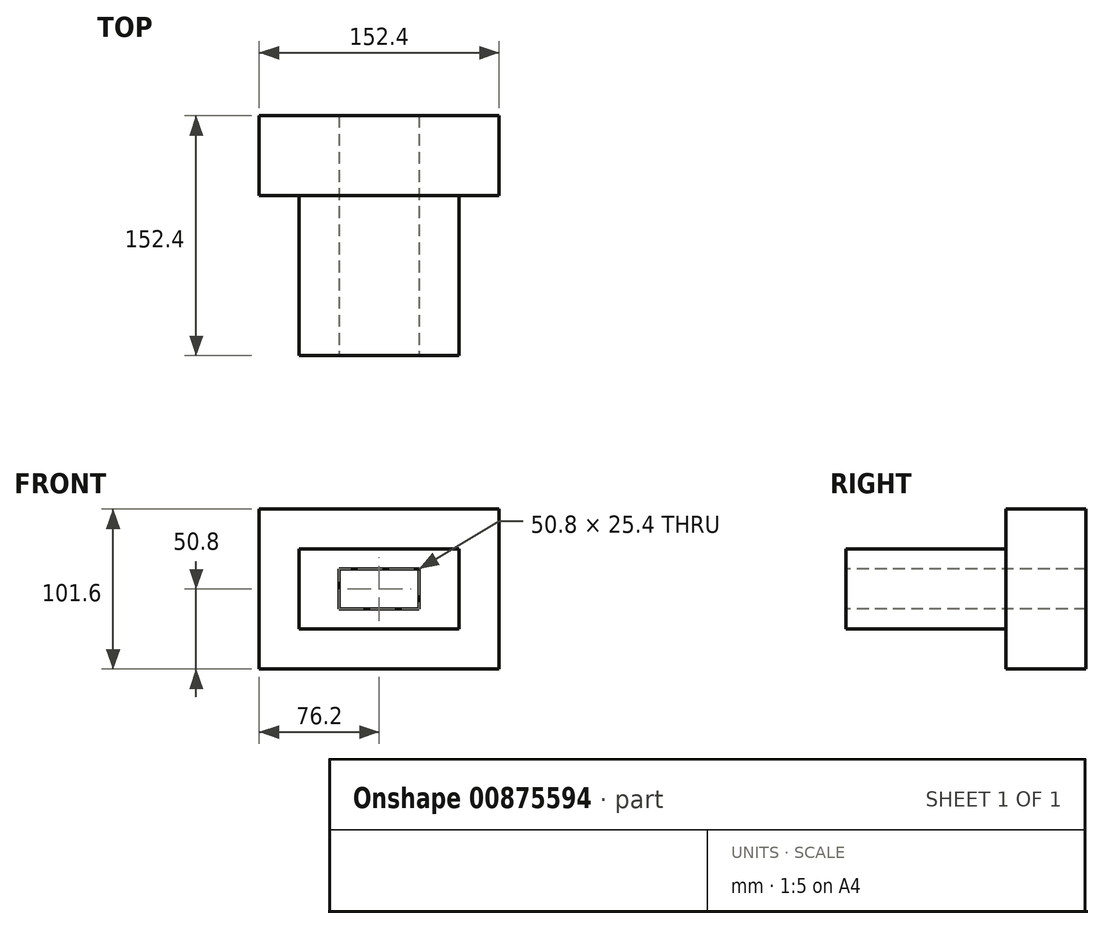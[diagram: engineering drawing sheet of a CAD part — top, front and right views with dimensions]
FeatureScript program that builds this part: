
annotation { "Feature Type Name" : "Feature", "Feature Type Description" : "" }
export const myFeature = defineFeature(function(context is Context, id is Id, definition is map)
    precondition{}
    {
        {
            var Q0;
            Q0=qCreatedBy(makeId("Front.planeOp"),FACE);
            var sketch = newSketch(context, id + "F0", { "sketchPlane" : qUnion([Q0])});
            skLineSegment(sketch, "E0.bottom", {"start": v(-76.2, 50.8) * mm, "end": v(76.2, 50.8) * mm});
            skLineSegment(sketch, "E0.top", {"start": v(-76.2, -50.8) * mm, "end": v(76.2, -50.8) * mm});
            skLineSegment(sketch, "E0.left", {"start": v(-76.2, 50.8) * mm, "end": v(-76.2, -50.8) * mm});
            skLineSegment(sketch, "E0.right", {"start": v(76.2, 50.8) * mm, "end": v(76.2, -50.8) * mm});
            skSolve(sketch);
        }
        {
            var Q0;
            Q0 = qSketchRegion(id + "F0", true);
            extrude(context, id + "F1", {"entities" : qUnion([Q0]), "depth" : 50.8 * mm, "offsetDistance" : 25.4 * mm});
        }
        {
            var Q0;
            Q0=makeQuery(id+"F1.opExtrude","CAP_FACE",FACE,{"disambiguationData":[OSD([sQuery(id+"F0.wireOp",EDGE,"E0.bottom"),sQuery(id+"F0.wireOp",EDGE,"E0.top"),sQuery(id+"F0.wireOp",EDGE,"E0.left"),sQuery(id+"F0.wireOp",EDGE,"E0.right")])],"isStart":false});
            var sketch = newSketch(context, id + "F2", { "sketchPlane" : qUnion([Q0])});
            skLineSegment(sketch, "E1.bottom", {"start": v(-25.4, 12.7) * mm, "end": v(25.4, 12.7) * mm});
            skLineSegment(sketch, "E1.top", {"start": v(-25.4, -12.7) * mm, "end": v(25.4, -12.7) * mm});
            skLineSegment(sketch, "E1.left", {"start": v(-25.4, 12.7) * mm, "end": v(-25.4, -12.7) * mm});
            skLineSegment(sketch, "E1.right", {"start": v(25.4, 12.7) * mm, "end": v(25.4, -12.7) * mm});
            skSolve(sketch);
        }
        {
            var Q0;
            Q0=makeQuery(id+"F2.imprint","IMPRINT",FACE,{"disambiguationData":[TD([[makeQuery(id+"F2.imprint","IMPRINT",EDGE,{"derivedFrom":sQuery(id+"F2.wireOp",EDGE,"E1.bottom")}),-1.0]])]});
            extrude(context, id + "F3", {"entities" : qUnion([Q0]), "operationType" : NewBodyOperationType.REMOVE, "endBound" : BoundingType.THROUGH_ALL, "oppositeDirection" : true, "depth" : 25.4 * mm, "offsetDistance" : 25.4 * mm});
        }
        {
            var Q0;
            Q0=makeQuery(id+"F1.opExtrude","CAP_FACE",FACE,{"disambiguationData":[OSD([sQuery(id+"F0.wireOp",EDGE,"E0.bottom"),sQuery(id+"F0.wireOp",EDGE,"E0.top"),sQuery(id+"F0.wireOp",EDGE,"E0.left"),sQuery(id+"F0.wireOp",EDGE,"E0.right")])],"isStart":false});
            var sketch = newSketch(context, id + "F4", { "sketchPlane" : qUnion([Q0])});
            skLineSegment(sketch, "E2.bottom", {"start": v(-50.8, 25.4) * mm, "end": v(50.8, 25.4) * mm});
            skLineSegment(sketch, "E2.top", {"start": v(-50.8, -25.4) * mm, "end": v(50.8, -25.4) * mm});
            skLineSegment(sketch, "E2.left", {"start": v(-50.8, 25.4) * mm, "end": v(-50.8, -25.4) * mm});
            skLineSegment(sketch, "E2.right", {"start": v(50.8, 25.4) * mm, "end": v(50.8, -25.4) * mm});
            skSolve(sketch);
        }
        {
            var Q0;
            Q0=makeQuery(id+"F4.imprint","IMPRINT",FACE,{"disambiguationData":[TD([[makeQuery(id+"F4.imprint","IMPRINT",EDGE,{"derivedFrom":sQuery(id+"F4.wireOp",EDGE,"E2.bottom")}),-1.0]])]});
            extrude(context, id + "F5", {"entities" : qUnion([Q0]), "operationType" : NewBodyOperationType.ADD, "depth" : 101.6 * mm, "offsetDistance" : 25.4 * mm});
        }
    });
